FCSTD DOCUMENT  (FreeCAD 1.0R39109 (Git))
Label: RearSightAssembly
License: All rights reserved
LicenseURL: http://en.wikipedia.org/wiki/All_rights_reserved
objects: App::Link×9, App::Part×2
EXTERNAL_REF file=RearSightBase.stl.FCStd obj=Part002
EXTERNAL_REF file=RearSightMid.stl.FCStd obj=Part
EXTERNAL_REF file=RearSightMarker.stl.FCStd obj=Part001
EXTERNAL_REF file=../../ReferenceParts/M3.FCStd obj=Part
EXTERNAL_REF file=../../ReferenceParts/M3.FCStd obj=Part003
EXTERNAL_REF file=../../ReferenceParts/M3.FCStd obj=Part004

FEATURE [App::Link] RearSightBase_stl  label="RearSightBase.stl"
  LinkedObject = -> <external RearSightBase.stl.FCStd>#Part002
FEATURE [App::Link] RearSightMid_stl  label="RearSightMid.stl"
  LinkPlacement = pos=(-27,4.76837e-07,-4) rot=(0,0,1;0rad)
  LinkedObject = -> <external RearSightMid.stl.FCStd>#Part
  Placement = pos=(-27,4.76837e-07,-4) rot=(0,0,1;0rad)
FEATURE [App::Link] RearSightMarker_stl  label="RearSightMarker.stl"
  LinkPlacement = pos=(-42,0,-4) rot=(0,1,0;1.5708rad)
  LinkedObject = -> <external RearSightMarker.stl.FCStd>#Part001
  Placement = pos=(-42,0,-4) rot=(0,1,0;1.5708rad)
FEATURE [App::Link] M3x10
  LinkPlacement = pos=(0,0,2.7) rot=(0,0,1;0rad)
  LinkedObject = -> <external ../../ReferenceParts/M3.FCStd>#Part
  Placement = pos=(0,0,2.7) rot=(0,0,1;0rad)
FEATURE [App::Link] M3Nylock
  LinkPlacement = pos=(0,0,1.7) rot=(1,0,0;3.14159rad)
  LinkedObject = -> <external ../../ReferenceParts/M3.FCStd>#Part003
  Placement = pos=(0,0,1.7) rot=(1,0,0;3.14159rad)
FEATURE [App::Link] M3x20
  LinkPlacement = pos=(27,-8,4) rot=(1,0,0;1.5708rad)
  LinkedObject = -> <external ../../ReferenceParts/M3.FCStd>#Part004
  Placement = pos=(27,-8,4) rot=(1,0,0;1.5708rad)
FEATURE [App::Link] M3x021
  LinkPlacement = pos=(-37,-8,1) rot=(1,0,0;1.5708rad)
  LinkedObject = -> <external ../../ReferenceParts/M3.FCStd>#Part004
  Placement = pos=(-37,-8,1) rot=(1,0,0;1.5708rad)
FEATURE [App::Link] M3Nylock001
  LinkPlacement = pos=(-37,8,1) rot=(-0.002789,0.707104,0.707104;3.13601rad)
  LinkedObject = -> <external ../../ReferenceParts/M3.FCStd>#Part003
  Placement = pos=(-37,8,1) rot=(-0.002789,0.707104,0.707104;3.13601rad)
FEATURE [App::Link] M3Nylock002
  LinkPlacement = pos=(27,8,4) rot=(-1,0,0;1.5708rad)
  LinkedObject = -> <external ../../ReferenceParts/M3.FCStd>#Part003
  Placement = pos=(27,8,4) rot=(-1,0,0;1.5708rad)
FEATURE [App::Part] Part001  label="Arm"
  Group = -> [M3x021,M3Nylock001,RearSightMarker_stl,RearSightMid_stl]
  Origin = -> Origin
  Placement = pos=(27,0,4) rot=(0,0,1;0rad)
FEATURE [App::Part] Part  label="RearSightAssembly"
  Group = -> [RearSightBase_stl,M3x10,M3Nylock,M3x20,M3Nylock002,Part001]
  Origin = -> Origin001

RESOLVED EXTERNAL PARTS (link-assembly join: the EXTERNAL_REF files above that resolve inside this repo's crawl, each included once):
---- part RearSightBase.stl.FCStd = doc fcstd_af10f3ed0e7a ----
FCSTD DOCUMENT  (FreeCAD 1.0R39109 (Git))
Label: RearSightBase.stl
License: All rights reserved
LicenseURL: http://en.wikipedia.org/wiki/All_rights_reserved
objects: Sketcher::SketchObject×6, PartDesign::Hole×3, PartDesign::Pad×2, PartDesign::Pocket×1, PartDesign::Mirrored×1, PartDesign::Body×1, App::Part×1
note: 33 computed .brp shape members not serialized (recipe doc carries the construction recipe); baked Part::Feature solids carry a one-line shape summary decoded from their .brp

FEATURE [Sketcher::SketchObject] Sketch008
  ArcFitTolerance = 1e-06
  AttachmentSupport = -> [XZ_Plane005]
  FullyConstrained = true
  MakeInternals = false
  MapMode = 5
  Placement = pos=(0,0,0) rot=(1,0,0;1.5708rad)
  sketch-geometry (4):
    g0: LineSegment StartX=-20 StartY=0 StartZ=0 EndX=-20 EndY=-10 EndZ=0
    g1: LineSegment StartX=-20 StartY=-10 StartZ=0 EndX=24.5 EndY=-10 EndZ=0
    g2: LineSegment StartX=24.5 StartY=-10 StartZ=0 EndX=29.5 EndY=0 EndZ=0
    g3: LineSegment StartX=29.5 StartY=0 StartZ=0 EndX=-20 EndY=0 EndZ=0
  constraints (12):
    c: Vertical(g0)
    c: Coincident(g0,g1)
    c: Horizontal(g1)
    c: Coincident(g1,g2)
    c: Coincident(g2,g3)
    c: Coincident(g3,g0)
    c: Horizontal(g3)
    c: DistanceX(g2,g2) = 5
    c: DistanceY(g2,g2) = 10
    c: DistanceX(g1,g1) = 44.5
    c: PointOnObject(g0,g-1)
    c: DistanceX(g0,g-1) = 20
FEATURE [PartDesign::Pad] Pad003
  Direction = (0,-1,2e-16)
  Length = 18
  Length2 = 10
  Midplane = true
  Placement = pos=(0,0,0) rot=(1,0,0;1.5708rad)
  Profile = -> Sketch008
  ReferenceAxis = -> Sketch008 [N_Axis]
  Refine = true
  Suppressed = false
  Type = 0
FEATURE [Sketcher::SketchObject] Sketch009
  ArcFitTolerance = 1e-06
  AttachmentOffset = pos=(0,0,9) rot=(0,0,1;0rad)
  AttachmentSupport = -> [XZ_Plane005]
  FullyConstrained = true
  MakeInternals = false
  MapMode = 5
  Placement = pos=(0,-9,2e-15) rot=(1,0,0;1.5708rad)
  sketch-geometry (7):
    g0: LineSegment StartX=31 StartY=6.5 StartZ=0 EndX=29.5 EndY=8 EndZ=0
    g1: LineSegment StartX=29.5 StartY=8 StartZ=0 EndX=12 EndY=8 EndZ=0
    g2: LineSegment StartX=12 StartY=8 StartZ=0 EndX=-1 EndY=-5 EndZ=0
    g3: LineSegment StartX=29.5 StartY=0 StartZ=0 EndX=31 EndY=1.5 EndZ=0
    g4: LineSegment StartX=31 StartY=1.5 StartZ=0 EndX=31 EndY=6.5 EndZ=0
    g5: LineSegment StartX=29.5 StartY=0 StartZ=0 EndX=26.6132 EndY=-5 EndZ=0
    g6: LineSegment StartX=26.6132 StartY=-5 StartZ=0 EndX=-1 EndY=-5 EndZ=0
  constraints (21):
    c: PointOnObject(g3,g-1)
    c: Coincident(g0,g1)
    c: Horizontal(g1)
    c: Coincident(g1,g2)
    c: DistanceX(g-1,g3) = 29.5
    c: DistanceY(g-1,g0) = 8
    c: Angle(g2,g1) = 2.35619
    c: Angle(g1,g0) = 2.35619
    c: Coincident(g4,g3)
    c: Coincident(g4,g0)
    c: Vertical(g4)
    c: Angle(g-1,g3) = 0.785398
    c: DistanceX(g-1,g3) = 31
    c: Vertical(g0,g3)
    c: Coincident(g5,g3)
    c: Coincident(g6,g5)
    c: Coincident(g6,g2)
    c: Horizontal(g6)
    c: DistanceY(g2,g-1) = 5
    c: DistanceX(g-1,g1) = 12
    c: Angle(g5,g-1) = 2.0944
FEATURE [Sketcher::SketchObject] Sketch010
  ArcFitTolerance = 1e-06
  AttachmentOffset = pos=(0,0,9) rot=(0,0,1;0rad)
  AttachmentSupport = -> [XZ_Plane005]
  FullyConstrained = true
  MakeInternals = false
  MapMode = 5
  Placement = pos=(0,-9,2e-15) rot=(1,0,0;1.5708rad)
  sketch-geometry (1):
    g0: Circle CenterX=27 CenterY=4 CenterZ=0 NormalX=0 NormalY=0 NormalZ=1 AngleXU=0 Radius=1.5
  constraints (3):
    c: DistanceX(g-1,g0) = 27
    c: DistanceY(g-1,g0) = 4
    c: Diameter(g0) = 3
FEATURE [Sketcher::SketchObject] Sketch011
  ArcFitTolerance = 1e-06
  AttachmentSupport = -> [XY_Plane005]
  FullyConstrained = true
  MakeInternals = false
  MapMode = 5
  sketch-geometry (1):
    g0: Circle CenterX=0 CenterY=0 CenterZ=0 NormalX=0 NormalY=0 NormalZ=1 AngleXU=0 Radius=1.6
  constraints (2):
    c: Coincident(g0,g-1)
    c: Diameter(g0) = 3.2
FEATURE [Sketcher::SketchObject] Sketch012
  ArcFitTolerance = 1e-06
  AttachmentSupport = -> [XZ_Plane005]
  FullyConstrained = true
  MakeInternals = false
  MapMode = 5
  Placement = pos=(0,0,0) rot=(1,0,0;1.5708rad)
  sketch-geometry (4):
    g0: ArcOfCircle CenterX=27 CenterY=4 CenterZ=0 NormalX=0 NormalY=0 NormalZ=1 AngleXU=0 Radius=4.5 StartAngle=4.81085 EndAngle=7.85398
    g1: LineSegment StartX=27.4423 StartY=-0.478206 StartZ=0 EndX=-18.3349 EndY=-5 EndZ=0
    g2: LineSegment StartX=-18.3349 StartY=-5 StartZ=0 EndX=-19.6684 EndY=8.5 EndZ=0
    g3: LineSegment StartX=-19.6684 StartY=8.5 StartZ=0 EndX=27 EndY=8.5 EndZ=0
  constraints (11):
    c: Coincident(g2,g1)
    c: Coincident(g3,g2)
    c: Horizontal(g3)
    c: Radius(g0) = 4.5
    c: DistanceY(g-1,g0) = 4
    c: DistanceX(g-1,g0) = 27
    c: DistanceY(g1,g-1) = 5
    c: Perpendicular(g1,g2)
    c: Distance(g1,g1) = 46
    c: Tangent(g3,g0) = 1.5708
    c: Tangent(g1,g0) = 1.5708
FEATURE [PartDesign::Pocket] Pocket003
  BaseFeature = -> Pad003
  Direction = (0,1,-2e-16)
  Length = 5
  Length2 = 5
  Midplane = true
  Placement = pos=(0,0,0) rot=(1,0,0;1.5708rad)
  Profile = -> Sketch012
  ReferenceAxis = -> Sketch012 [N_Axis]
  Refine = true
  Suppressed = false
  Type = 1
FEATURE [PartDesign::Pad] Pad004  label="Ears"
  BaseFeature = -> Pocket003
  Direction = (0,-1,2e-16)
  Length = 3.8
  Length2 = 10
  Placement = pos=(0,0,0) rot=(1,0,0;1.5708rad)
  Profile = -> Sketch009
  ReferenceAxis = -> Sketch009 [N_Axis]
  Refine = true
  Reversed = true
  Suppressed = false
  Type = 0
FEATURE [PartDesign::Hole] Hole002
  BaseFeature = -> Pad004
  CustomThreadClearance = 0
  Depth = 25
  DepthType = 0
  Diameter = 3.4
  DrillForDepth = false
  DrillPoint = 1
  DrillPointAngle = 118
  HoleCutCountersinkAngle = 90
  HoleCutCustomValues = false
  HoleCutDepth = 1
  HoleCutDiameter = 6.5
  HoleCutType = 1
  ModelThread = false
  Placement = pos=(0,0,0) rot=(1,0,0;1.5708rad)
  Profile = -> Sketch010
  Refine = true
  Suppressed = false
  Tapered = false
  TaperedAngle = 90
  ThreadClass = 0
  ThreadDepth = 25
  ThreadDepthType = 0
  ThreadDirection = 0
  ThreadFit = 0
  ThreadSize = 9
  ThreadType = 1
  Threaded = false
  UseCustomThreadClearance = false
FEATURE [PartDesign::Mirrored] Mirrored001
  BaseFeature = -> Hole002
  MirrorPlane = -> XZ_Plane005
  Originals = -> [Pad004,Hole002]
  Placement = pos=(0,0,0) rot=(1,0,0;1.5708rad)
  Refine = true
  Suppressed = false
  TransformMode = 0
FEATURE [PartDesign::Hole] Hole003  label="HeightAsjustmentHole"
  BaseFeature = -> Mirrored001
  CustomThreadClearance = 0
  Depth = 25
  DepthType = 0
  Diameter = 2.5
  DrillForDepth = false
  DrillPoint = 1
  DrillPointAngle = 118
  HoleCutCountersinkAngle = 90
  HoleCutCustomValues = false
  HoleCutDepth = 5.5
  HoleCutDiameter = 8
  HoleCutType = 1
  ModelThread = false
  Placement = pos=(0,0,0) rot=(1,0,0;1.5708rad)
  Profile = -> Sketch011
  Refine = true
  Suppressed = false
  Tapered = false
  TaperedAngle = 90
  ThreadClass = 0
  ThreadDepth = 25
  ThreadDepthType = 0
  ThreadDirection = 0
  ThreadFit = 2
  ThreadSize = 9
  ThreadType = 1
  Threaded = true
  UseCustomThreadClearance = false
FEATURE [Sketcher::SketchObject] Sketch013
  ArcFitTolerance = 1e-06
  AttachmentOffset = pos=(0,0,10) rot=(0,0,1;0rad)
  AttachmentSupport = -> [XY_Plane005]
  FullyConstrained = true
  MakeInternals = false
  MapMode = 5
  Placement = pos=(0,0,10) rot=(0,0,1;0rad)
  sketch-geometry (2):
    g0: Circle CenterX=-15 CenterY=5 CenterZ=0 NormalX=0 NormalY=0 NormalZ=1 AngleXU=0 Radius=1.5
    g1: Circle CenterX=20 CenterY=-5 CenterZ=0 NormalX=0 NormalY=0 NormalZ=1 AngleXU=0 Radius=1.5
  constraints (6):
    c: DistanceX(g0,g1) = 35
    c: Distance(g0,g-1) = 5
    c: DistanceX(g0,g-1) = 15
    c: Distance(g1,g-1) = 5
    c: Equal(g1,g0)
    c: Diameter(g0) = 3
FEATURE [PartDesign::Hole] Hole004  label="MountToFrameHoles"
  BaseFeature = -> Hole003
  CustomThreadClearance = 0
  Depth = 25
  DepthType = 0
  Diameter = 3.4
  DrillForDepth = false
  DrillPoint = 1
  DrillPointAngle = 118
  HoleCutCountersinkAngle = 90
  HoleCutCustomValues = false
  HoleCutDepth = 18
  HoleCutDiameter = 6.5
  HoleCutType = 1
  ModelThread = false
  Placement = pos=(0,0,0) rot=(1,0,0;1.5708rad)
  Profile = -> Sketch013
  Refine = true
  Suppressed = false
  Tapered = false
  TaperedAngle = 90
  ThreadClass = 0
  ThreadDepth = 25
  ThreadDepthType = 0
  ThreadDirection = 0
  ThreadFit = 0
  ThreadSize = 9
  ThreadType = 1
  Threaded = false
  UseCustomThreadClearance = false
FEATURE [PartDesign::Body] Body002  label="RearSightBase"
  AllowCompound = false
  Group = -> [Sketch008,Pad003,Sketch009,Pocket003,Pad004,Sketch010,Hole002,Mirrored001,Sketch011,Hole003,Sketch012,Sketch013,Hole004]
  Origin = -> Origin005
  Tip = -> Hole004
FEATURE [App::Part] Part002  label="RearSightBase.stl"
  Group = -> [Body002]
  Origin = -> Origin004
---- part RearSightMarker.stl.FCStd = doc fcstd_6140b5d60d7d ----
FCSTD DOCUMENT  (FreeCAD 1.0R39109 (Git))
Label: RearSightMarker.stl
License: All rights reserved
LicenseURL: http://en.wikipedia.org/wiki/All_rights_reserved
objects: Sketcher::SketchObject×4, PartDesign::Pad×2, PartDesign::Pocket×2, PartDesign::Body×1, App::Part×1
note: 21 computed .brp shape members not serialized (recipe doc carries the construction recipe); baked Part::Feature solids carry a one-line shape summary decoded from their .brp

FEATURE [Sketcher::SketchObject] Sketch004
  ArcFitTolerance = 1e-06
  AttachmentSupport = -> [XY_Plane003]
  FullyConstrained = true
  MakeInternals = false
  MapMode = 5
  sketch-geometry (4):
    g0: LineSegment StartX=-15 StartY=9 StartZ=0 EndX=-15 EndY=-9 EndZ=0
    g1: LineSegment StartX=-15 StartY=-9 StartZ=0 EndX=0 EndY=-9 EndZ=0
    g2: LineSegment StartX=0 StartY=-9 StartZ=0 EndX=0 EndY=9 EndZ=0
    g3: LineSegment StartX=0 StartY=9 StartZ=0 EndX=-15 EndY=9 EndZ=0
  constraints (12):
    c: Coincident(g0,g1)
    c: Coincident(g2,g3)
    c: Coincident(g3,g0)
    c: Vertical(g0)
    c: Vertical(g2)
    c: Horizontal(g1)
    c: Horizontal(g3)
    c: Coincident(g2,g1)
    c: DistanceY(g0,g-1) = 9
    c: DistanceY(g-1,g0) = 9
    c: DistanceX(g0,g-1) = 15
    c: PointOnObject(g2,g-2)
FEATURE [PartDesign::Pad] Pad001
  Direction = (0,0,1)
  Length = 2
  Length2 = 10
  Profile = -> Sketch004
  ReferenceAxis = -> Sketch004 [N_Axis]
  Refine = true
  Reversed = true
  Suppressed = false
  Type = 0
FEATURE [Sketcher::SketchObject] Sketch005
  ArcFitTolerance = 1e-06
  AttachmentSupport = -> [XZ_Plane003]
  FullyConstrained = true
  MakeInternals = false
  MapMode = 5
  Placement = pos=(0,0,0) rot=(1,0,0;1.5708rad)
  sketch-geometry (9):
    g0: LineSegment StartX=-9 StartY=-1 StartZ=0 EndX=-8 EndY=8.8 EndZ=0
    g1: LineSegment StartX=-8 StartY=8.8 StartZ=0 EndX=-3.2 EndY=8.8 EndZ=0
    g2: LineSegment StartX=-3.2 StartY=8.8 StartZ=0 EndX=-1.2 EndY=6.8 EndZ=0
    g3: LineSegment StartX=-1.2 StartY=6.8 StartZ=0 EndX=-1.2 EndY=3.1 EndZ=0
    g4: LineSegment [constr] StartX=-1.2 StartY=3.1 StartZ=0 EndX=-3 EndY=1.3 EndZ=0
    g5: LineSegment StartX=-3.5 StartY=-1 StartZ=0 EndX=-9 EndY=-1 EndZ=0
    g6: Circle [constr] CenterX=-5 CenterY=5 CenterZ=0 NormalX=0 NormalY=0 NormalZ=1 AngleXU=0 Radius=3.5
    g7: LineSegment StartX=-1.2 StartY=3.1 StartZ=0 EndX=-3.5 EndY=0.8 EndZ=0
    g8: LineSegment StartX=-3.5 StartY=0.8 StartZ=0 EndX=-3.5 EndY=-1 EndZ=0
  constraints (27):
    c: Horizontal(g1)
    c: Coincident(g1,g2)
    c: Coincident(g2,g3)
    c: Vertical(g3)
    c: Coincident(g3,g4)
    c: Coincident(g5,g0)
    c: Horizontal(g5)
    c: DistanceY(g5,g-1) = 1
    c: DistanceX(g5,g-1) = 3.5
    c: Diameter(g6) = 7
    c: DistanceX(g6,g-1) = 5
    c: DistanceY(g-1,g6) = 5
    c: DistanceY(g6,g1) = 3.8
    c: Coincident(g0,g1)
    c: DistanceX(g0,g-1) = 8
    c: DistanceX(g6,g2) = 3.8
    c: DistanceY(g4,g6) = 3.7
    c: DistanceX(g6,g4) = 2
    c: Angle(g-1,g4) = 0.785398
    c: DistanceY(g2,g1) = 2
    c: Angle(g3,g2) = 0.785398
    c: Coincident(g7,g3)
    c: Coincident(g8,g7)
    c: Coincident(g8,g5)
    c: PointOnObject(g4,g7)
    c: Vertical(g8)
    c: DistanceX(g0,g-1) = 9
FEATURE [PartDesign::Pad] Pad002
  BaseFeature = -> Pad001
  Direction = (0,-1,2e-16)
  Length = 4
  Length2 = 10
  Midplane = true
  Profile = -> Sketch005
  ReferenceAxis = -> Sketch005 [N_Axis]
  Refine = true
  Suppressed = false
  Type = 0
FEATURE [Sketcher::SketchObject] Sketch006
  ArcFitTolerance = 1e-06
  AttachmentSupport = -> [XZ_Plane003]
  FullyConstrained = true
  MakeInternals = false
  MapMode = 5
  Placement = pos=(0,0,0) rot=(1,0,0;1.5708rad)
  sketch-geometry (1):
    g0: Circle CenterX=-5 CenterY=5 CenterZ=0 NormalX=0 NormalY=0 NormalZ=1 AngleXU=0 Radius=1.25
  constraints (3):
    c: Diameter(g0) = 2.5
    c: DistanceX(g0,g-1) = 5
    c: DistanceY(g-1,g0) = 5
FEATURE [PartDesign::Pocket] Pocket001
  BaseFeature = -> Pad002
  Direction = (0,1,-2e-16)
  Length = 5
  Length2 = 5
  Midplane = true
  Profile = -> Sketch006
  ReferenceAxis = -> Sketch006 [N_Axis]
  Refine = true
  Suppressed = false
  Type = 1
FEATURE [Sketcher::SketchObject] Sketch015
  ArcFitTolerance = 1e-06
  AttachmentOffset = pos=(0,0,-2) rot=(0,0,1;0rad)
  AttachmentSupport = -> [XY_Plane003]
  FullyConstrained = true
  MakeInternals = false
  MapMode = 5
  Placement = pos=(0,0,-2) rot=(0,0,1;0rad)
  sketch-geometry (4):
    g0: LineSegment StartX=-15 StartY=3 StartZ=0 EndX=-15 EndY=-3 EndZ=0
    g1: LineSegment StartX=-15 StartY=-3 StartZ=0 EndX=-12 EndY=-3 EndZ=0
    g2: LineSegment StartX=-12 StartY=-3 StartZ=0 EndX=-12 EndY=3 EndZ=0
    g3: LineSegment StartX=-12 StartY=3 StartZ=0 EndX=-15 EndY=3 EndZ=0
  constraints (11):
    c: Coincident(g0,g1)
    c: Coincident(g1,g2)
    c: Coincident(g2,g3)
    c: Coincident(g3,g0)
    c: Vertical(g0)
    c: Horizontal(g1)
    c: Horizontal(g3)
    c: DistanceX(g0,g-1) = 15
    c: DistanceY(g2,g2) = 6
    c: Symmetric(g1,g2,g-1)
    c: DistanceX(g1,g1) = 3
FEATURE [PartDesign::Pocket] Pocket006  label="Notch"
  BaseFeature = -> Pocket001
  Direction = (0,0,-1)
  Length = 2
  Length2 = 5
  Profile = -> Sketch015
  ReferenceAxis = -> Sketch015 [N_Axis]
  Refine = true
  Reversed = true
  Suppressed = false
  TaperAngle = 30
  Type = 0
FEATURE [PartDesign::Body] Body001
  AllowCompound = false
  Group = -> [Sketch004,Pad001,Sketch005,Pad002,Sketch006,Pocket001,Sketch015,Pocket006]
  Origin = -> Origin003
  Tip = -> Pocket006
FEATURE [App::Part] Part001  label="RearSightMarker.stl"
  Group = -> [Body001]
  Origin = -> Origin002
  Placement = pos=(-15,0,-3.3e-15) rot=(0,1,0;0rad)
---- part RearSightMid.stl.FCStd = doc fcstd_c3b8c093f147 ----
FCSTD DOCUMENT  (FreeCAD 1.0R39109 (Git))
Label: RearSightMid.stl
License: All rights reserved
LicenseURL: http://en.wikipedia.org/wiki/All_rights_reserved
objects: Sketcher::SketchObject×6, PartDesign::Pocket×4, PartDesign::Pad×1, PartDesign::Hole×1, PartDesign::Mirrored×1, PartDesign::Body×1, App::Part×1
note: 33 computed .brp shape members not serialized (recipe doc carries the construction recipe); baked Part::Feature solids carry a one-line shape summary decoded from their .brp

FEATURE [Sketcher::SketchObject] Sketch
  ArcFitTolerance = 1e-06
  AttachmentSupport = -> [XY_Plane001]
  FullyConstrained = true
  MakeInternals = false
  MapMode = 5
  sketch-geometry (12):
    g0: LineSegment StartX=-15 StartY=9 StartZ=0 EndX=-15 EndY=-9 EndZ=0
    g1: LineSegment StartX=-15 StartY=-9 StartZ=0 EndX=-4.82843 EndY=-9 EndZ=0
    g2: LineSegment StartX=-3.41421 StartY=-8.41421 StartZ=0 EndX=-4e-16 EndY=-5 EndZ=0
    g3: LineSegment StartX=-15 StartY=9 StartZ=0 EndX=-4.82843 EndY=9 EndZ=0
    g4: LineSegment StartX=-3.41421 StartY=8.41421 StartZ=0 EndX=-4e-16 EndY=5 EndZ=0
    g5: ArcOfCircle CenterX=-4.82843 CenterY=7 CenterZ=0 NormalX=0 NormalY=0 NormalZ=1 AngleXU=0 Radius=2 StartAngle=0.785398 EndAngle=1.5708
    g6: GeomPoint [constr] X=-4 Y=9 Z=0
    g7: ArcOfCircle CenterX=-4.82843 CenterY=-7 CenterZ=0 NormalX=0 NormalY=0 NormalZ=1 AngleXU=0 Radius=2 StartAngle=4.71239 EndAngle=5.49779
    g8: GeomPoint [constr] X=-4 Y=-9 Z=0
    g9: LineSegment StartX=-4e-16 StartY=5 StartZ=0 EndX=32 EndY=5 EndZ=0
    g10: LineSegment StartX=32 StartY=5 StartZ=0 EndX=32 EndY=-5 EndZ=0
    g11: LineSegment StartX=32 StartY=-5 StartZ=0 EndX=0 EndY=-5 EndZ=0
  constraints (32):
    c: Vertical(g0)
    c: DistanceX(g0,g-1) = 15
    c: Coincident(g1,g0)
    c: Horizontal(g1)
    c: PointOnObject(g2,g-2)
    c: Coincident(g3,g0)
    c: Horizontal(g3)
    c: PointOnObject(g4,g-2)
    c: Vertical(g6,g8)
    c: PointOnObject(g6,g3)
    c: PointOnObject(g6,g4)
    c: Tangent(g3,g5) = 1.5708
    c: Tangent(g4,g5) = 1.5708
    c: PointOnObject(g8,g1)
    c: PointOnObject(g8,g2)
    c: Tangent(g1,g7) = -1.5708
    c: Tangent(g2,g7) = -1.5708
    c: Radius(g5) = 2
    c: Angle(g-1,g2) = 0.785398
    c: Vertical(g7,g5)
    c: Coincident(g9,g4)
    c: Horizontal(g9)
    c: Coincident(g10,g9)
    c: Vertical(g10)
    c: Coincident(g11,g10)
    c: Coincident(g11,g2)
    c: Horizontal(g11)
    c: DistanceY(g-1,g9) = 5
    c: DistanceY(g10,g-1) = 5
    c: DistanceX(g-1,g9) = 32
    c: DistanceY(g-1,g0) = 9
    c: DistanceY(g0,g-1) = 9
FEATURE [PartDesign::Pad] Pad
  Direction = (0,0,1)
  Length = 14
  Length2 = 10
  Profile = -> Sketch
  ReferenceAxis = -> Sketch [N_Axis]
  Refine = true
  Suppressed = false
  Type = 0
FEATURE [Sketcher::SketchObject] Sketch001
  ArcFitTolerance = 1e-06
  AttachmentOffset = pos=(0,0,10) rot=(0,0,1;0rad)
  AttachmentSupport = -> [XY_Plane001]
  FullyConstrained = true
  MakeInternals = false
  MapMode = 5
  Placement = pos=(0,0,10) rot=(0,0,1;0rad)
  sketch-geometry (4):
    g0: ArcOfCircle CenterX=-1.5 CenterY=-5.257e-13 CenterZ=0 NormalX=0 NormalY=0 NormalZ=1 AngleXU=0 Radius=1.5 StartAngle=1.5708 EndAngle=4.71239
    g1: ArcOfCircle CenterX=1.5 CenterY=1.133e-13 CenterZ=0 NormalX=0 NormalY=0 NormalZ=1 AngleXU=0 Radius=1.5 StartAngle=4.71239 EndAngle=7.85398
    g2: LineSegment StartX=-1.5 StartY=1.5 StartZ=0 EndX=1.5 EndY=1.5 EndZ=0
    g3: LineSegment StartX=-1.5 StartY=-1.5 StartZ=0 EndX=1.5 EndY=-1.5 EndZ=0
  constraints (9):
    c: Tangent(g0,g2) = 1.5708
    c: Tangent(g0,g3) = -1.5708
    c: Tangent(g1,g2) = 1.5708
    c: Tangent(g1,g3) = -1.5708
    c: Equal(g0,g1)
    c: Horizontal(g3)
    c: Radius(g1) = 1.5
    c: Distance(g2,g2) = 3
    c: Symmetric(g0,g1,g-1)
FEATURE [Sketcher::SketchObject] Sketch002
  ArcFitTolerance = 1e-06
  AttachmentOffset = pos=(0,0,9) rot=(0,0,1;0rad)
  AttachmentSupport = -> [XZ_Plane001]
  FullyConstrained = true
  MakeInternals = false
  MapMode = 5
  Placement = pos=(0,-9,2e-15) rot=(1,0,0;1.5708rad)
  sketch-geometry (1):
    g0: Circle CenterX=-10 CenterY=5 CenterZ=0 NormalX=0 NormalY=0 NormalZ=1 AngleXU=0 Radius=1.5
  constraints (3):
    c: DistanceY(g-1,g0) = 5
    c: DistanceX(g0,g-1) = 10
    c: Diameter(g0) = 3
FEATURE [Sketcher::SketchObject] Sketch003
  ArcFitTolerance = 1e-06
  AttachmentSupport = -> [XZ_Plane001]
  FullyConstrained = true
  MakeInternals = false
  MapMode = 5
  Placement = pos=(0,0,0) rot=(1,0,0;1.5708rad)
  sketch-geometry (9):
    g0: LineSegment StartX=-6 StartY=1 StartZ=0 EndX=-12 EndY=1 EndZ=0
    g1: LineSegment StartX=-12 StartY=1 StartZ=0 EndX=-14 EndY=3 EndZ=0
    g2: LineSegment StartX=-14 StartY=3 StartZ=0 EndX=-15 EndY=3 EndZ=0
    g3: LineSegment StartX=-15 StartY=3 StartZ=0 EndX=-15 EndY=20 EndZ=0
    g4: LineSegment StartX=-15 StartY=20 StartZ=0 EndX=10 EndY=20 EndZ=0
    g5: Circle [constr] CenterX=-10 CenterY=5 CenterZ=0 NormalX=0 NormalY=0 NormalZ=1 AngleXU=0 Radius=1.5
    g6: LineSegment StartX=-6 StartY=1 StartZ=0 EndX=-6 EndY=8 EndZ=0
    g7: LineSegment StartX=-6 StartY=8 StartZ=0 EndX=10 EndY=8 EndZ=0
    g8: LineSegment StartX=10 StartY=8 StartZ=0 EndX=10 EndY=20 EndZ=0
  constraints (27):
    c: Horizontal(g0)
    c: Coincident(g1,g2)
    c: Coincident(g2,g3)
    c: Vertical(g3)
    c: Coincident(g3,g4)
    c: Horizontal(g4)
    c: DistanceY(g-1,g4) = 20
    c: Angle(g1,g0) = 0.785398
    c: Horizontal(g2)
    c: DistanceX(g2,g-1) = 15
    c: DistanceX(g5,g-1) = 10
    c: DistanceY(g-1,g5) = 5
    c: DistanceY(g2,g5) = 2
    c: DistanceX(g1,g5) = 4
    c: DistanceY(g0,g5) = 4
    c: DistanceX(g5,g0) = 4
    c: Diameter(g5) = 3
    c: Coincident(g0,g1)
    c: Coincident(g6,g0)
    c: Vertical(g6)
    c: Coincident(g7,g6)
    c: Horizontal(g7)
    c: Coincident(g8,g7)
    c: Coincident(g8,g4)
    c: Vertical(g8)
    c: DistanceX(g-1,g4) = 10
    c: DistanceY(g-1,g7) = 8
FEATURE [Sketcher::SketchObject] Sketch007
  ArcFitTolerance = 1e-06
  AttachmentSupport = -> [XZ_Plane001]
  FullyConstrained = true
  MakeInternals = false
  MapMode = 5
  Placement = pos=(0,0,0) rot=(1,0,0;1.5708rad)
  sketch-geometry (10):
    g0: Circle CenterX=27 CenterY=4 CenterZ=0 NormalX=0 NormalY=0 NormalZ=1 AngleXU=0 Radius=1.6
    g1: ArcOfCircle CenterX=27 CenterY=4 CenterZ=0 NormalX=0 NormalY=0 NormalZ=1 AngleXU=0 Radius=4 StartAngle=4.71238 EndAngle=7.85398
    g2: LineSegment StartX=27 StartY=8 StartZ=0 EndX=-5 EndY=8 EndZ=0
    g3: LineSegment StartX=-15 StartY=20 StartZ=0 EndX=37 EndY=20 EndZ=0
    g4: LineSegment StartX=37 StartY=20 StartZ=0 EndX=37 EndY=-2 EndZ=0
    g5: LineSegment StartX=37 StartY=-2 StartZ=0 EndX=27 EndY=-2 EndZ=0
    g6: LineSegment StartX=27 StartY=-2 StartZ=0 EndX=27 EndY=4.50671e-11 EndZ=0
    g7: LineSegment StartX=-15 StartY=20 StartZ=0 EndX=-15 EndY=11 EndZ=0
    g8: LineSegment StartX=-15 StartY=11 StartZ=0 EndX=-13 EndY=11 EndZ=0
    g9: LineSegment StartX=-13 StartY=11 StartZ=0 EndX=-5 EndY=8 EndZ=0
  constraints (29):
    c: Diameter(g0) = 3.2
    c: DistanceX(g-1,g0) = 27
    c: DistanceY(g-1,g0) = 4
    c: Coincident(g1,g0)
    c: PointOnObject(g1,g-1)
    c: Tangent(g1,g2) = -1.5708
    c: Coincident(g3,g4)
    c: Vertical(g4)
    c: Coincident(g4,g5)
    c: Horizontal(g5)
    c: Coincident(g5,g6)
    c: Coincident(g6,g1)
    c: Vertical(g6)
    c: DistanceY(g-1,g2) = 8
    c: Horizontal(g3)
    c: Radius(g1) = 4
    c: DistanceY(g6,g6) = 2
    c: DistanceX(g5,g4) = 10
    c: DistanceY(g-1,g3) = 20
    c: Coincident(g8,g7)
    c: DistanceX(g3,g-1) = 15
    c: Coincident(g7,g3)
    c: DistanceY(g-1,g7) = 11
    c: Horizontal(g8)
    c: Coincident(g9,g8)
    c: Coincident(g9,g2)
    c: DistanceX(g2,g-1) = 5
    c: DistanceX(g8,g8) = 2
    c: Vertical(g7)
FEATURE [PartDesign::Pocket] Pocket004  label="AdjusterBoltHole"
  BaseFeature = -> Pad
  Direction = (0,0,-1)
  Length = 5
  Length2 = 5
  Midplane = true
  Profile = -> Sketch001
  ReferenceAxis = -> Sketch001 [N_Axis]
  Refine = true
  Suppressed = false
  Type = 1
FEATURE [Sketcher::SketchObject] Sketch014
  ArcFitTolerance = 1e-06
  AttachmentOffset = pos=(0,0,1) rot=(0,0,1;0rad)
  AttachmentSupport = -> [XY_Plane001]
  FullyConstrained = true
  MakeInternals = false
  MapMode = 5
  Placement = pos=(0,0,1) rot=(0,0,1;0rad)
  sketch-geometry (4):
    g0: ArcOfCircle CenterX=-1.5 CenterY=-8.8e-15 CenterZ=0 NormalX=0 NormalY=0 NormalZ=1 AngleXU=0 Radius=3.5 StartAngle=1.5708 EndAngle=4.71239
    g1: ArcOfCircle CenterX=1.5 CenterY=8.7e-15 CenterZ=0 NormalX=0 NormalY=0 NormalZ=1 AngleXU=0 Radius=3.5 StartAngle=4.71239 EndAngle=7.85398
    g2: LineSegment StartX=-1.5 StartY=3.5 StartZ=0 EndX=1.5 EndY=3.5 EndZ=0
    g3: LineSegment StartX=-1.5 StartY=-3.5 StartZ=0 EndX=1.5 EndY=-3.5 EndZ=0
  constraints (9):
    c: Tangent(g0,g2) = 1.5708
    c: Tangent(g0,g3) = -1.5708
    c: Tangent(g1,g2) = 1.5708
    c: Tangent(g1,g3) = -1.5708
    c: Equal(g0,g1)
    c: Horizontal(g3)
    c: Radius(g1) = 3.5
    c: DistanceX(g2,g2) = 3
    c: Symmetric(g1,g0,g-1)
FEATURE [PartDesign::Pocket] Pocket005  label="AdjusterBoltHeadHole"
  BaseFeature = -> Pocket004
  Direction = (0,0,-1)
  Length = 5
  Length2 = 5
  Profile = -> Sketch014
  ReferenceAxis = -> Sketch014 [N_Axis]
  Refine = true
  Reversed = true
  Suppressed = false
  Type = 1
FEATURE [PartDesign::Hole] Hole001
  BaseFeature = -> Pocket005
  CustomThreadClearance = 0
  Depth = 25
  DepthType = 0
  Diameter = 3.2
  DrillForDepth = false
  DrillPoint = 1
  DrillPointAngle = 118
  HoleCutCountersinkAngle = 90
  HoleCutCustomValues = false
  HoleCutDepth = 1
  HoleCutDiameter = 7
  HoleCutType = 1
  ModelThread = false
  Profile = -> Sketch002
  Refine = true
  Suppressed = false
  Tapered = false
  TaperedAngle = 90
  ThreadClass = 0
  ThreadDepth = 25
  ThreadDepthType = 0
  ThreadDirection = 0
  ThreadFit = 1
  ThreadSize = 9
  ThreadType = 1
  Threaded = false
  UseCustomThreadClearance = false
FEATURE [PartDesign::Mirrored] Mirrored
  BaseFeature = -> Hole001
  MirrorPlane = -> XZ_Plane001
  Originals = -> [Hole001]
  Refine = true
  Suppressed = false
  TransformMode = 0
FEATURE [PartDesign::Pocket] Pocket
  BaseFeature = -> Mirrored
  Direction = (0,1,-2e-16)
  Length = 12
  Length2 = 5
  Midplane = true
  Profile = -> Sketch003
  ReferenceAxis = -> Sketch003 [N_Axis]
  Refine = true
  Suppressed = false
  Type = 0
FEATURE [PartDesign::Pocket] Pocket002
  BaseFeature = -> Pocket
  Direction = (0,1,-2e-16)
  Length = 5
  Length2 = 5
  Midplane = true
  Profile = -> Sketch007
  ReferenceAxis = -> Sketch007 [N_Axis]
  Refine = true
  Suppressed = false
  Type = 1
FEATURE [PartDesign::Body] Body
  AllowCompound = false
  Group = -> [Sketch,Pad,Sketch001,Sketch002,Pocket004,Sketch014,Pocket005,Hole001,Mirrored,Sketch003,Pocket,Sketch007,Pocket002]
  Origin = -> Origin001
  Tip = -> Pocket002
FEATURE [App::Part] Part  label="RearSightMid.stl"
  Group = -> [Body]
  Origin = -> Origin
